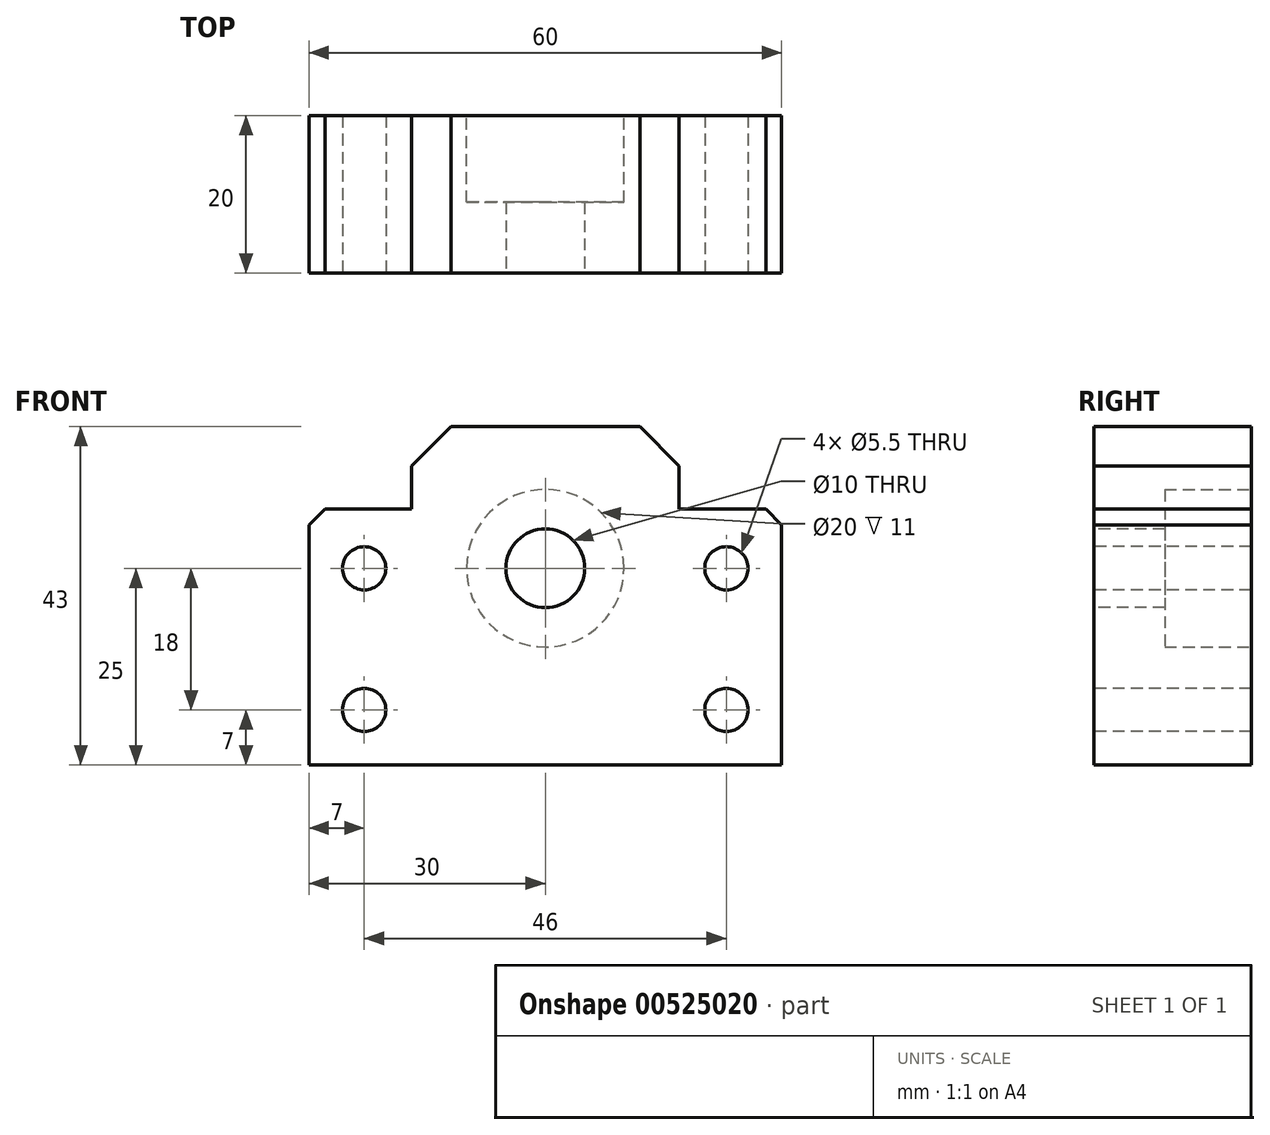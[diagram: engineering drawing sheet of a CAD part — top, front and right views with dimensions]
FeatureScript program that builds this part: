
annotation { "Feature Type Name" : "Feature", "Feature Type Description" : "" }
export const myFeature = defineFeature(function(context is Context, id is Id, definition is map)
    precondition{}
    {
        {
            var Q0;
            Q0=qCreatedBy(makeId("Front.planeOp"),FACE);
            var sketch = newSketch(context, id + "F0", { "sketchPlane" : qUnion([Q0])});
            skLineSegment(sketch, "E0.bottom", {"start": v(17, 21.5) * mm, "end": v(-17, 21.5) * mm});
            skLineSegment(sketch, "E0.top", {"start": v(30, -21.5) * mm, "end": v(-30, -21.5) * mm});
            skLineSegment(sketch, "E0.left", {"start": v(30, 11) * mm, "end": v(30, -21.5) * mm});
            skLineSegment(sketch, "E0.right", {"start": v(-30, 11) * mm, "end": v(-30, -21.5) * mm});
            skPoint(sketch, "E0.middle", {"position": v(0, 0) * mm});
            skLineSegment(sketch, "E1", {"start": v(-17, 21.5) * mm, "end": v(-17, 11) * mm});
            skLineSegment(sketch, "E2", {"start": v(-17, 11) * mm, "end": v(-30, 11) * mm});
            skLineSegment(sketch, "E3", {"start": v(17, 21.5) * mm, "end": v(17, 11) * mm});
            skLineSegment(sketch, "E4", {"start": v(17, 11) * mm, "end": v(30, 11) * mm});
            skPoint(sketch, "E5.orphan", {"position": v(-30, 21.5) * mm});
            skPoint(sketch, "E6.orphan", {"position": v(30, 21.5) * mm});
            skPoint(sketch, "E7.center.orphan", {"position": v(0, 3.5) * mm});
            skPoint(sketch, "E8.center.orphan", {"position": v(23, 3.5) * mm});
            skPoint(sketch, "E9.center.orphan", {"position": v(23, -14.5) * mm});
            skPoint(sketch, "E10.center.orphan", {"position": v(-23, 3.5) * mm});
            skPoint(sketch, "E11.center.orphan", {"position": v(-23, -14.14) * mm});
            skSolve(sketch);
        }
        {
            var Q0;
            Q0 = qSketchRegion(id + "F0", true);
            extrude(context, id + "F1", {"entities" : qUnion([Q0]), "endBound" : BoundingType.SYMMETRIC, "depth" : 20 * mm, "offsetDistance" : 25 * mm});
        }
        {
            var Q0;
            Q0=makeQuery(id+"F1.opExtrude","CAP_FACE",FACE,{"disambiguationData":[OSD([sQuery(id+"F0.wireOp",EDGE,"E0.bottom"),sQuery(id+"F0.wireOp",EDGE,"E0.top"),sQuery(id+"F0.wireOp",EDGE,"E0.left"),sQuery(id+"F0.wireOp",EDGE,"E0.right"),sQuery(id+"F0.wireOp",EDGE,"E1"),sQuery(id+"F0.wireOp",EDGE,"E2"),sQuery(id+"F0.wireOp",EDGE,"E3"),sQuery(id+"F0.wireOp",EDGE,"E4")])],"isStart":false});
            var sketch = newSketch(context, id + "F2", { "sketchPlane" : qUnion([Q0])});
            skCircle(sketch, "E12", {"center": v(0, 3.5) * mm, "radius": 5 * mm});
            skCircle(sketch, "E13", {"center": v(23, 3.5) * mm, "radius": 2.75 * mm});
            skCircle(sketch, "E14", {"center": v(23, -14.5) * mm, "radius": 2.75 * mm});
            skCircle(sketch, "E15", {"center": v(-23, -14.5) * mm, "radius": 2.75 * mm});
            skCircle(sketch, "E16", {"center": v(-23, 3.5) * mm, "radius": 2.75 * mm});
            skSolve(sketch);
        }
        {
            var Q0;
            Q0 = qSketchRegion(id + "F2", true);
            extrude(context, id + "F3", {"entities" : qUnion([Q0]), "operationType" : NewBodyOperationType.REMOVE, "oppositeDirection" : true, "depth" : 20 * mm, "offsetDistance" : 25 * mm});
        }
        {
            var Q0;
            Q0=makeQuery(id+"F1.opExtrude","SWEPT_EDGE",EDGE,{"disambiguationData":[OSD([sQuery(id+"F0.wireOp",EDGE,"E0.bottom"),sQuery(id+"F0.wireOp",EDGE,"E1")])]});
            var Q1;
            Q1=makeQuery(id+"F1.opExtrude","SWEPT_EDGE",EDGE,{"disambiguationData":[OSD([sQuery(id+"F0.wireOp",EDGE,"E0.bottom"),sQuery(id+"F0.wireOp",EDGE,"E3")])]});
            chamfer(context, id + "F4", {"entities" : qUnion([Q0, Q1]), "width" : 5 * mm, "tangentPropagation" : true});
        }
        {
            var Q0;
            Q0=makeQuery(id+"F1.opExtrude","SWEPT_EDGE",EDGE,{"disambiguationData":[OSD([sQuery(id+"F0.wireOp",EDGE,"E0.left"),sQuery(id+"F0.wireOp",EDGE,"E4")])]});
            var Q1;
            Q1=makeQuery(id+"F1.opExtrude","SWEPT_EDGE",EDGE,{"disambiguationData":[OSD([sQuery(id+"F0.wireOp",EDGE,"E0.right"),sQuery(id+"F0.wireOp",EDGE,"E2")])]});
            chamfer(context, id + "F5", {"entities" : qUnion([Q0, Q1]), "width" : 2 * mm, "tangentPropagation" : true});
        }
        {
            var Q0;
            Q0=makeQuery(id+"F1.opExtrude","CAP_FACE",FACE,{"disambiguationData":[OSD([sQuery(id+"F0.wireOp",EDGE,"E0.bottom"),sQuery(id+"F0.wireOp",EDGE,"E0.top"),sQuery(id+"F0.wireOp",EDGE,"E0.left"),sQuery(id+"F0.wireOp",EDGE,"E0.right"),sQuery(id+"F0.wireOp",EDGE,"E1"),sQuery(id+"F0.wireOp",EDGE,"E2"),sQuery(id+"F0.wireOp",EDGE,"E3"),sQuery(id+"F0.wireOp",EDGE,"E4")])],"isStart":true});
            var sketch = newSketch(context, id + "F6", { "sketchPlane" : qUnion([Q0])});
            skCircle(sketch, "E17", {"center": v(0, 3.5) * mm, "radius": 10 * mm});
            skSolve(sketch);
        }
        {
            var Q0;
            Q0 = qSketchRegion(id + "F6", true);
            extrude(context, id + "F7", {"entities" : qUnion([Q0]), "operationType" : NewBodyOperationType.REMOVE, "oppositeDirection" : true, "depth" : 11 * mm, "offsetDistance" : 25 * mm});
        }
    });
